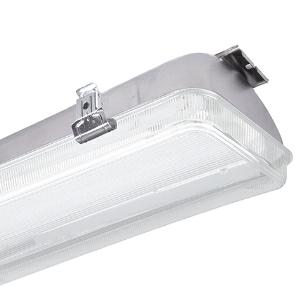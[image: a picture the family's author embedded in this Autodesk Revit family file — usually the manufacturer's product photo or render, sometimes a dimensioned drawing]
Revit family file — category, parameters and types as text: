
# Revit family: 3f_filippi_-_beta_235_92_pc_ampio_3f_filippi_-_52940_-_beta_235_led_921x25_ampio_l655
name_source: partatom
category: Lighting Fixtures
units: mm (PartAtom-declared; Revit-internal decimal feet)

## family parameters
Cut with Voids When Loaded = No
Host = Face
Light Source = No
Part Type = Normal
Room Calculation Point = No
Round Connector Dimension = Use Diameter
Shared = No

## types (1)
- 3F Filippi - Beta 235 92 PC Ampio (1 x LED, 4073 lm, 27.5 W, 4000 K)
    Apparent Load = 28 VA
    Approval mark = CE
    CIE Flux Codes = 60 88 98 97 100
    Color Rendering = 80
    Color Temperature = 4000 K
    Control Gear = Electronic ballast
    Default Elevation = 1800 mm
    Description = ILLUMINOTECHNICAL
Luminous efficiency 100% (DLOR 99%, ULOR 1%).
Initial luminous flux of the luminaire 4073 lm.
Wide symmetric distribution.
Installation Interdistance Transv.D = 1.25 x hu - Long.D = 1.44 x hu.
Tabular UGR (CIE 117 - 4H-8H; S=0.25H; 70/50/20): RUG 19.2 - 19.6.
Beam angle: 91° - 102°.
Luminous efficacy 148 lm/W.
Lifetime (L93/B10): 30000 h. (tq+25°C)
Lifetime (L90/B10): 50000 h. (tq+25°C)
Lifetime (L85/B10): 80000 h. (tq+25°C)
Lifetime (L80/B10): 100000 h. (tq+25°C)
Lifetime (L85/B10): 50000 h. (tq+45°C)
Sudden decreased luminous flux after 50000 hours: 0% (C0).
Photobiological safety in compliance with IEC/TR 62778: RG0 risk exempt, (IEC 62471).
In compliance with IEC/EN 62722-2-1 - IEC/EN 62717 standards.

SOURCE
Linear LED module 25W/840.
Energy efficiency class (UE 2019/2020 - UE 2019/2015): C.
CIE 13.3 Colour rendering index: CRI >80 (R9 <50%).
IES TM-30 Fidelity Index: Rf = 84 Rg = 95.
CCT nominal colour temperature 4000 K.
Colour initial tolerance (MacAdam): SDCM 3.

MECHANICAL
Housing in AISI 304 stainless steel, pressed in one single piece.
Polycarbonate screen etched internally, V2 self-extinguishing, UV stabilised, injection moulded.
Ecologic anti-aging sealing gasket.
Oversized gear-tray reflector unit in highly reflective white painted hot-galvanised steel.
Methacrylate (PMMA) lenses with external flat surface.
Stainless steel safety snap-lock clips for diffuser mounting.
Luminaire with limited surface temperature. - D - (EN 60598-2-24)
Dimensions: 655x235 mm, height 140 mm. Weight 3.56 kg.
IP65 protection degree.
Mechanical strength to impacts IK10 (20 joule).
Glow-wire test resistance 850°C.

ELECTRICAL
Halogen Free electronic wiring 230V-50/60Hz, power factor 0.90, THD <25%, constant output current, class I, 1 driver.
Power of the luminaire 27.5 W.
ENEC - CE.
Flicker: <4%.
Luminaire compliant with EN 60598-2-22 for power supply from a centralised emergency system CPSS (Central Power Supply System), not incorporated in the luminaire - high risk areas excluded. The default power and flux are 100% in AC and 100% in DC.
Ambient temperature from -20°C to +45°C.
Temperature class T6 max 85°C.
Quick connection via M20 3P connector with 9-13 mm tightening range.
Relative humidity UR: <85%.

INSTALLATION
Ceiling / Suspended / Wall.
All accessories dedicated to this product are available on the Catalog and on our website www.3F-Filippi.com.

APPLICATIONS
Suitable product for food production plants (HACCP), IFS (Food Version 6), BRC (GSFS Food Version 7).
Dry, dusty indoor environments, subject to occasional water splashes.
Any environments except the ones where the luminaire materials are unsuitable.
Industrial environments, warehouses, environments where security locks are required on all clips, e.g. prisons.
Environments in which it is necessary a total protection against falling fragments (eg environments with foodstuffs or machines with moving parts or with extreme temperature changes), use luminaires with laminated glass.
Tempered glass is not immune to falling fragments from harmless and caused by shocks or exceptionally derived from the tempering process.

WARNING
Fixture not suitable for cold stores with an ambient temperature <0°C and/or relative humidity >85%.
Luminaire designed for disposal/recycling at end-of-life.
Replaceable (LED only) light source by a professional. Replaceable control gear by a professional.
    Height = 140 mm  [stored 0.459318 ft]
    Lamp = 1 x LED
    Lamp Light Flux = 4073 lm
    Lamp Power = 27.5 W
    Lamp count = 1
    Length = 655 mm
    Lifetime = 50000 h
    Luminous efficacy = 148 lm/W
    Manufacturer = 3F Filippi
    ModVariant = No
    Model = 3F Filippi - 52940 - Beta 235 LED 921x25 AMPIO L655
    Mounting Place = Ceiling
    Mounting Type = Pendant
    Number of Poles = 1
    OnlyDefault = Yes
    Power Factor = 1
    Product Name = 3F Filippi - Beta 235 92 PC Ampio
    Product group = pendant luminaire
    ProductGroupID = 9
    Protection Class = Protection class I
    Protection Degree = IP 65
    RLX_Detail_Level = 1
    RLX_Emergency_Light_Flux = 0 lm
    RLX_Emergency_Type = 0
    RLX_Emergency_Type_DB = No
    RlxData = <blob elided: 89253 chars, md5=e53fb4ec>
    Socket = socket
    Standby Power = 0 W
    System Light Flux = 4073 lm
    System Power = 28 W
    Type Comments = Product without accessories
    Type Image = 3ffilippi_52940.jpg
    URL = http://relux.com
    VarID = ---
    Voltage = 0 V
    Weight = 0.00 kg
    Width = 235 mm

note: [stored X ft] marks values corroborated as IEEE doubles in the binary element streams (Revit-internal decimal feet)

## geometry (parser evidence)
native form markers: Blend x4, Sweep x12
no freeform markers — native parametric forms only
